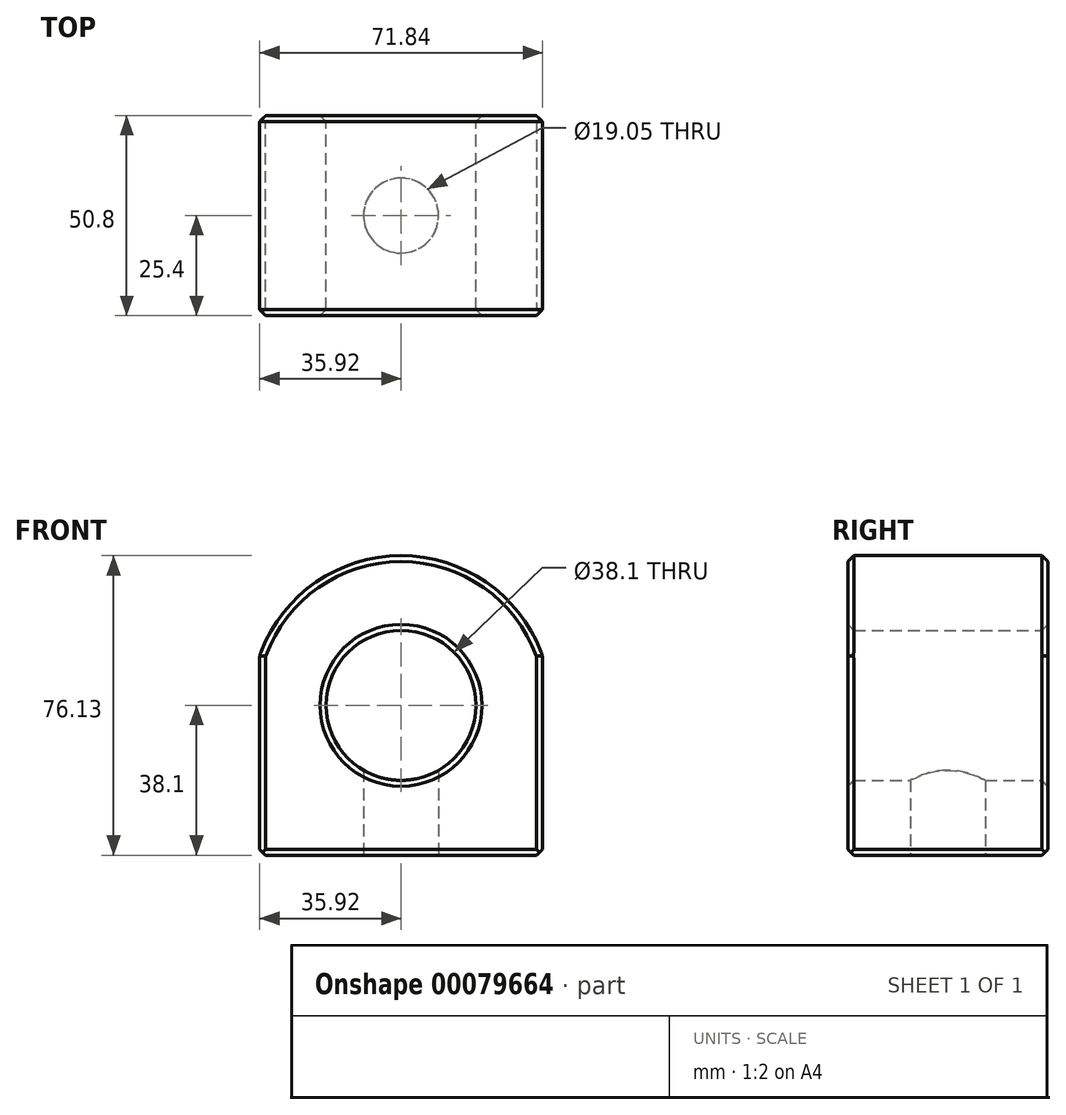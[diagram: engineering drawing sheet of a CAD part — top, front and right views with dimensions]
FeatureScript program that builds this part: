
annotation { "Feature Type Name" : "Feature", "Feature Type Description" : "" }
export const myFeature = defineFeature(function(context is Context, id is Id, definition is map)
    precondition{}
    {
        {
            var Q0;
            Q0=qCreatedBy(makeId("Front.planeOp"),FACE);
            var sketch = newSketch(context, id + "F0", { "sketchPlane" : qUnion([Q0])});
            skCircle(sketch, "E0", {"center": v(0, 0) * mm, "radius": 38.1 * mm, "construction": true});
            skLineSegment(sketch, "E1", {"start": v(-42.22, 12.7) * mm, "end": v(44.34, 12.7) * mm, "construction": true});
            skArc(sketch, "E2", {"start": v(35.92, 12.7) * mm, "mid": v(0, 38.03) * mm, "end": v(-35.92, 12.7) * mm});
            skLineSegment(sketch, "E3", {"start": v(-35.92, 12.7) * mm, "end": v(-35.92, -38.1) * mm});
            skLineSegment(sketch, "E4", {"start": v(35.92, 12.7) * mm, "end": v(35.92, -38.1) * mm});
            skLineSegment(sketch, "E5", {"start": v(-35.92, -38.1) * mm, "end": v(35.92, -38.1) * mm});
            skCircle(sketch, "E6", {"center": v(0, 0) * mm, "radius": 19.05 * mm});
            skSolve(sketch);
        }
        {
            var Q0;
            Q0 = qSketchRegion(id + "F0", true);
            extrude(context, id + "F1", {"entities" : qUnion([Q0]), "depth" : 50.8 * mm});
        }
        {
            var Q0;
            Q0=makeQuery(id+"F1.opExtrude","SWEPT_FACE",FACE,{"disambiguationData":[OSD([sQuery(id+"F0.wireOp",EDGE,"E5")])]});
            var sketch = newSketch(context, id + "F2", { "sketchPlane" : qUnion([Q0])});
            skCircle(sketch, "E7", {"center": v(0, 25.4) * mm, "radius": 9.53 * mm});
            skSolve(sketch);
        }
        {
            var Q0;
            Q0=makeQuery(id+"F2.imprint","IMPRINT",FACE,{"disambiguationData":[TD([[makeQuery(id+"F2.imprint","IMPRINT",EDGE,{"derivedFrom":sQuery(id+"F2.wireOp",EDGE,"E7")}),1.0]])]});
            extrude(context, id + "F3", {"entities" : qUnion([Q0]), "operationType" : NewBodyOperationType.REMOVE, "oppositeDirection" : true, "depth" : 25.4 * mm});
        }
        {
            var Q0;
            Q0=makeQuery(id+"F1.opExtrude","CAP_EDGE",EDGE,{"disambiguationData":[OSD([sQuery(id+"F0.wireOp",EDGE,"E2")])],"isStart":false});
            var Q1;
            Q1=makeQuery(id+"F1.opExtrude","CAP_FACE",FACE,{"disambiguationData":[OSD([sQuery(id+"F0.wireOp",EDGE,"E2"),sQuery(id+"F0.wireOp",EDGE,"E3"),sQuery(id+"F0.wireOp",EDGE,"E4"),sQuery(id+"F0.wireOp",EDGE,"E5"),sQuery(id+"F0.wireOp",EDGE,"E6")])],"isStart":false});
            chamfer(context, id + "F4", {"entities" : qUnion([Q0, Q1]), "width" : 1.52 * mm, "tangentPropagation" : true});
        }
        {
            var Q0;
            Q0=makeQuery(id+"F1.opExtrude","CAP_EDGE",EDGE,{"disambiguationData":[OSD([sQuery(id+"F0.wireOp",EDGE,"E2")])],"isStart":true});
            var Q1;
            Q1=makeQuery(id+"F1.opExtrude","CAP_EDGE",EDGE,{"disambiguationData":[OSD([sQuery(id+"F0.wireOp",EDGE,"E4")])],"isStart":true});
            var Q2;
            Q2=makeQuery(id+"F1.opExtrude","CAP_EDGE",EDGE,{"disambiguationData":[OSD([sQuery(id+"F0.wireOp",EDGE,"E5")])],"isStart":true});
            var Q3;
            Q3=makeQuery(id+"F1.opExtrude","CAP_EDGE",EDGE,{"disambiguationData":[OSD([sQuery(id+"F0.wireOp",EDGE,"E3")])],"isStart":true});
            var Q4;
            Q4=makeQuery(id+"F1.opExtrude","CAP_EDGE",EDGE,{"disambiguationData":[OSD([sQuery(id+"F0.wireOp",EDGE,"E6")])],"isStart":true});
            chamfer(context, id + "F5", {"entities" : qUnion([Q0, Q1, Q2, Q3, Q4]), "width" : 1.52 * mm, "tangentPropagation" : true});
        }
        {
            var Q0;
            Q0=makeQuery(id+"F1.opExtrude","SWEPT_EDGE",EDGE,{"disambiguationData":[OSD([sQuery(id+"F0.wireOp",EDGE,"E4"),sQuery(id+"F0.wireOp",EDGE,"E5")])]});
            var Q1;
            Q1=makeQuery(id+"F1.opExtrude","SWEPT_EDGE",EDGE,{"disambiguationData":[OSD([sQuery(id+"F0.wireOp",EDGE,"E3"),sQuery(id+"F0.wireOp",EDGE,"E5")])]});
            var Q2;
            Q2=makeQuery(id+"F3.boolean.opBoolean","COPY",EDGE,{"derivedFrom":makeQuery(id+"F3.opExtrude","CAP_EDGE",EDGE,{"disambiguationData":[OSD([sQuery(id+"F2.wireOp",EDGE,"E7")])],"isStart":true})});
            chamfer(context, id + "F6", {"entities" : qUnion([Q0, Q1, Q2]), "width" : 1.52 * mm, "tangentPropagation" : true});
        }
        {
            var Q0;
            Q0=makeQuery(id+"F1.opExtrude","SWEPT_EDGE",EDGE,{"disambiguationData":[OSD([sQuery(id+"F0.wireOp",EDGE,"E2"),sQuery(id+"F0.wireOp",EDGE,"E3")])]});
            fillet(context, id + "F7", {"entities" : qUnion([Q0]), "radius" : 5.08 * mm, "tangentPropagation" : true, "allowEdgeOverflow" : false});
        }
        {
            var Q0;
            Q0=makeQuery(id+"F1.opExtrude","SWEPT_EDGE",EDGE,{"disambiguationData":[OSD([sQuery(id+"F0.wireOp",EDGE,"E2"),sQuery(id+"F0.wireOp",EDGE,"E4")])]});
            fillet(context, id + "F8", {"entities" : qUnion([Q0]), "radius" : 5.08 * mm, "tangentPropagation" : true, "allowEdgeOverflow" : false});
        }
    });
